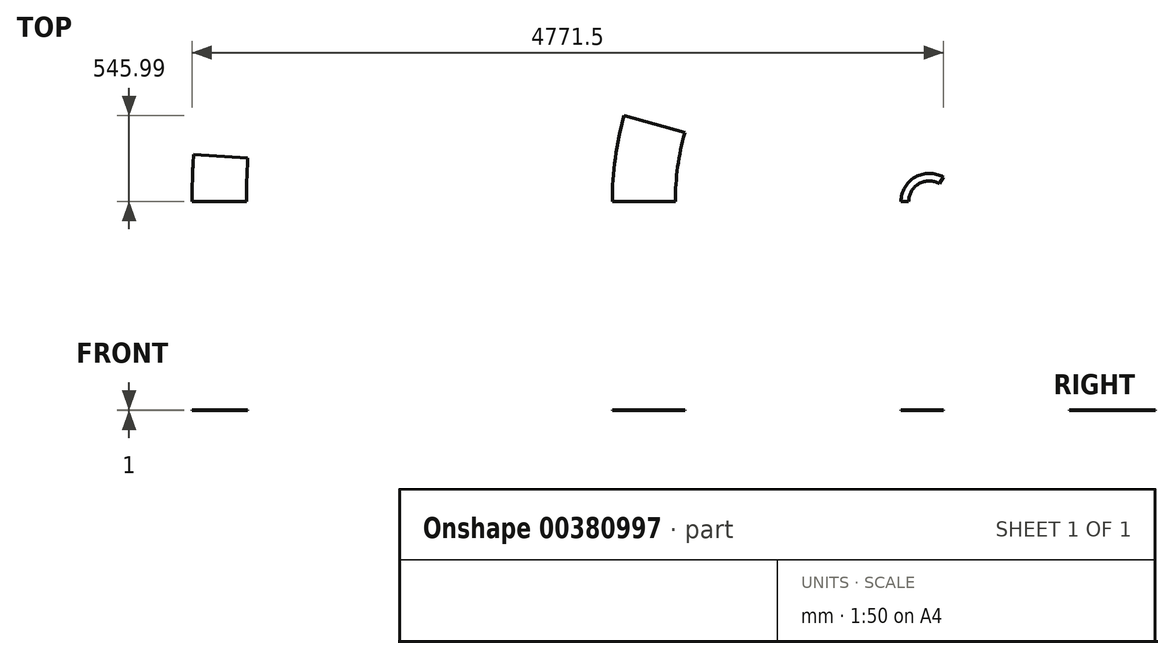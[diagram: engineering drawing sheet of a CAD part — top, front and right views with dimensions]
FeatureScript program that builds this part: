
annotation { "Feature Type Name" : "Feature", "Feature Type Description" : "" }
export const myFeature = defineFeature(function(context is Context, id is Id, definition is map)
    precondition{}
    {
        {
            var Q0;
            Q0=qCreatedBy(makeId("Top.planeOp"),FACE);
            var sketch = newSketch(context, id + "F0", { "sketchPlane" : qUnion([Q0])});
            skLineSegment(sketch, "E0", {"start": v(0, 0) * mm, "end": v(-131, 0) * mm, "construction": true});
            skLineSegment(sketch, "E1", {"start": v(-131, 0) * mm, "end": v(-179, 0) * mm});
            skLineSegment(sketch, "E2", {"start": v(0, 0) * mm, "end": v(89.5, 155.02) * mm, "construction": true});
            skArc(sketch, "E3", {"start": v(65.5, 113.45) * mm, "mid": v(-65.5, 113.45) * mm, "end": v(-131, 0) * mm});
            skArc(sketch, "E4", {"start": v(89.5, 155.02) * mm, "mid": v(-89.5, 155.02) * mm, "end": v(-179, 0) * mm});
            skLineSegment(sketch, "E5", {"start": v(65.5, 113.45) * mm, "end": v(89.5, 155.02) * mm});
            skSolve(sketch);
        }
        {
            var Q0;
            Q0=qCreatedBy(makeId("Top.planeOp"),FACE);
            var sketch = newSketch(context, id + "F1", { "sketchPlane" : qUnion([Q0])});
            skLineSegment(sketch, "E6", {"start": v(0, 0) * mm, "end": v(-4337, 0) * mm, "construction": true});
            skLineSegment(sketch, "E7", {"start": v(-4337, 0) * mm, "end": v(-4682, 0) * mm});
            skLineSegment(sketch, "E8", {"start": v(0, 0) * mm, "end": v(-4672.5, 298.06) * mm, "construction": true});
            skArc(sketch, "E9", {"start": v(-4328.2, 276.1) * mm, "mid": v(-4334.8, 138.12) * mm, "end": v(-4337, 0) * mm});
            skArc(sketch, "E10", {"start": v(-4672.5, 298.06) * mm, "mid": v(-4679.63, 149.1) * mm, "end": v(-4682, 0) * mm});
            skLineSegment(sketch, "E11", {"start": v(-4328.2, 276.1) * mm, "end": v(-4672.5, 298.06) * mm});
            skSolve(sketch);
        }
        {
            var Q0;
            Q0=qCreatedBy(makeId("Top.planeOp"),FACE);
            var sketch = newSketch(context, id + "F2", { "sketchPlane" : qUnion([Q0])});
            skArc(sketch, "E12", {"start": v(-75, 0) * mm, "mid": v(29.9, 68.78) * mm, "end": v(51.15, -54.85) * mm});
            skArc(sketch, "E13", {"start": v(-127, 0) * mm, "mid": v(50.64, 116.47) * mm, "end": v(86.61, -92.88) * mm});
            skLineSegment(sketch, "E14", {"start": v(-75, 0) * mm, "end": v(-127, 0) * mm});
            skLineSegment(sketch, "E15", {"start": v(51.15, -54.85) * mm, "end": v(86.61, -92.88) * mm});
            skSolve(sketch);
        }
        {
            var Q0;
            Q0=qCreatedBy(makeId("Top.planeOp"),FACE);
            var sketch = newSketch(context, id + "F3", { "sketchPlane" : qUnion([Q0])});
            skArc(sketch, "E16", {"start": v(-3023, 0) * mm, "mid": v(-3012.55, 251.12) * mm, "end": v(-2981.28, 500.5) * mm});
            skArc(sketch, "E17", {"start": v(-3363.5, 0) * mm, "mid": v(-3351.88, 279.4) * mm, "end": v(-3317.08, 556.87) * mm});
            skLineSegment(sketch, "E18", {"start": v(-3023, 0) * mm, "end": v(-3363.5, 0) * mm});
            skLineSegment(sketch, "E19", {"start": v(-2981.28, 500.5) * mm, "end": v(-3317.08, 556.87) * mm});
            skSolve(sketch);
        }
        {
            var Q0;
            Q0=qCreatedBy(makeId("Top.planeOp"),FACE);
            var sketch = newSketch(context, id + "F4", { "sketchPlane" : qUnion([Q0])});
            skArc(sketch, "E20", {"start": v(-53, 0) * mm, "mid": v(33, 41.48) * mm, "end": v(11.92, -51.64) * mm});
            skArc(sketch, "E21", {"start": v(-125, 0) * mm, "mid": v(77.81, 97.83) * mm, "end": v(28.12, -121.8) * mm});
            skLineSegment(sketch, "E22", {"start": v(-53, 0) * mm, "end": v(-125, 0) * mm});
            skLineSegment(sketch, "E23", {"start": v(11.92, -51.64) * mm, "end": v(28.12, -121.8) * mm});
            skSolve(sketch);
        }
        {
            var Q0;
            Q0=qCreatedBy(makeId("Top.planeOp"),FACE);
            var sketch = newSketch(context, id + "F5", { "sketchPlane" : qUnion([Q0])});
            skArc(sketch, "E24", {"start": v(-1467, 0) * mm, "mid": v(-1462.15, 119.23) * mm, "end": v(-1447.62, 237.68) * mm});
            skArc(sketch, "E25", {"start": v(-2567.5, 0) * mm, "mid": v(-2559, 208.68) * mm, "end": v(-2533.58, 415.98) * mm});
            skLineSegment(sketch, "E26", {"start": v(-1467, 0) * mm, "end": v(-2567.5, 0) * mm});
            skLineSegment(sketch, "E27", {"start": v(-1447.62, 237.68) * mm, "end": v(-2533.58, 415.98) * mm});
            skSolve(sketch);
        }
        {
            var Q0;
            Q0=makeQuery(id+"F0.imprint","IMPRINT",FACE,{"disambiguationData":[TD([[makeQuery(id+"F0.imprint","IMPRINT",EDGE,{"derivedFrom":sQuery(id+"F0.wireOp",EDGE,"E1")}),-1.0]])]});
            var Q1;
            Q1=makeQuery(id+"F2.imprint","IMPRINT",FACE,{"disambiguationData":[TD([[makeQuery(id+"F2.imprint","IMPRINT",EDGE,{"derivedFrom":sQuery(id+"F2.wireOp",EDGE,"E12")}),1.0]])]});
            var Q2;
            Q2=makeQuery(id+"F4.imprint","IMPRINT",FACE,{"disambiguationData":[TD([[makeQuery(id+"F4.imprint","IMPRINT",EDGE,{"derivedFrom":sQuery(id+"F4.wireOp",EDGE,"E20")}),1.0]])]});
            var Q3;
            Q3=makeQuery(id+"F5.imprint","IMPRINT",FACE,{"disambiguationData":[TD([[makeQuery(id+"F5.imprint","IMPRINT",EDGE,{"derivedFrom":sQuery(id+"F5.wireOp",EDGE,"E24")}),1.0]])]});
            var Q4;
            Q4=makeQuery(id+"F3.imprint","IMPRINT",FACE,{"disambiguationData":[TD([[makeQuery(id+"F3.imprint","IMPRINT",EDGE,{"derivedFrom":sQuery(id+"F3.wireOp",EDGE,"E16")}),1.0]])]});
            var Q5;
            Q5=makeQuery(id+"F1.imprint","IMPRINT",FACE,{"disambiguationData":[TD([[makeQuery(id+"F1.imprint","IMPRINT",EDGE,{"derivedFrom":sQuery(id+"F1.wireOp",EDGE,"E7")}),-1.0]])]});
            var Q6;
            Q6 = qSketchRegion(id + "F7", true);
            extrude(context, id + "F6", {"entities" : qUnion([Q0, Q1, Q2, Q3, Q4, Q5, Q6]), "depth" : 1 * mm});
        }
        {
            var Q0;
            Q0=qCreatedBy(makeId("Top.planeOp"),FACE);
            var sketch = newSketch(context, id + "F7", { "sketchPlane" : qUnion([Q0])});
            skLineSegment(sketch, "E28", {"start": v(-1612.9, 0) * mm, "end": v(-2013.34, 0) * mm});
            skLineSegment(sketch, "E29", {"start": v(-1552.46, 437.4) * mm, "end": v(-1937.9, 546) * mm});
            skArc(sketch, "E30", {"start": v(-1552.46, 437.4) * mm, "mid": v(-1597.72, 220.78) * mm, "end": v(-1612.9, 0) * mm});
            skArc(sketch, "E31", {"start": v(-1937.9, 546) * mm, "mid": v(-1994.39, 275.6) * mm, "end": v(-2013.34, 0) * mm});
            skSolve(sketch);
        }
        {
            var Q0;
            Q0=makeQuery(id+"F7.imprint","IMPRINT",FACE,{"disambiguationData":[TD([[makeQuery(id+"F7.imprint","IMPRINT",EDGE,{"derivedFrom":sQuery(id+"F7.wireOp",EDGE,"E28")}),-1.0]])]});
            extrude(context, id + "F8", {"entities" : qUnion([Q0]), "depth" : 1 * mm});
        }
    });
